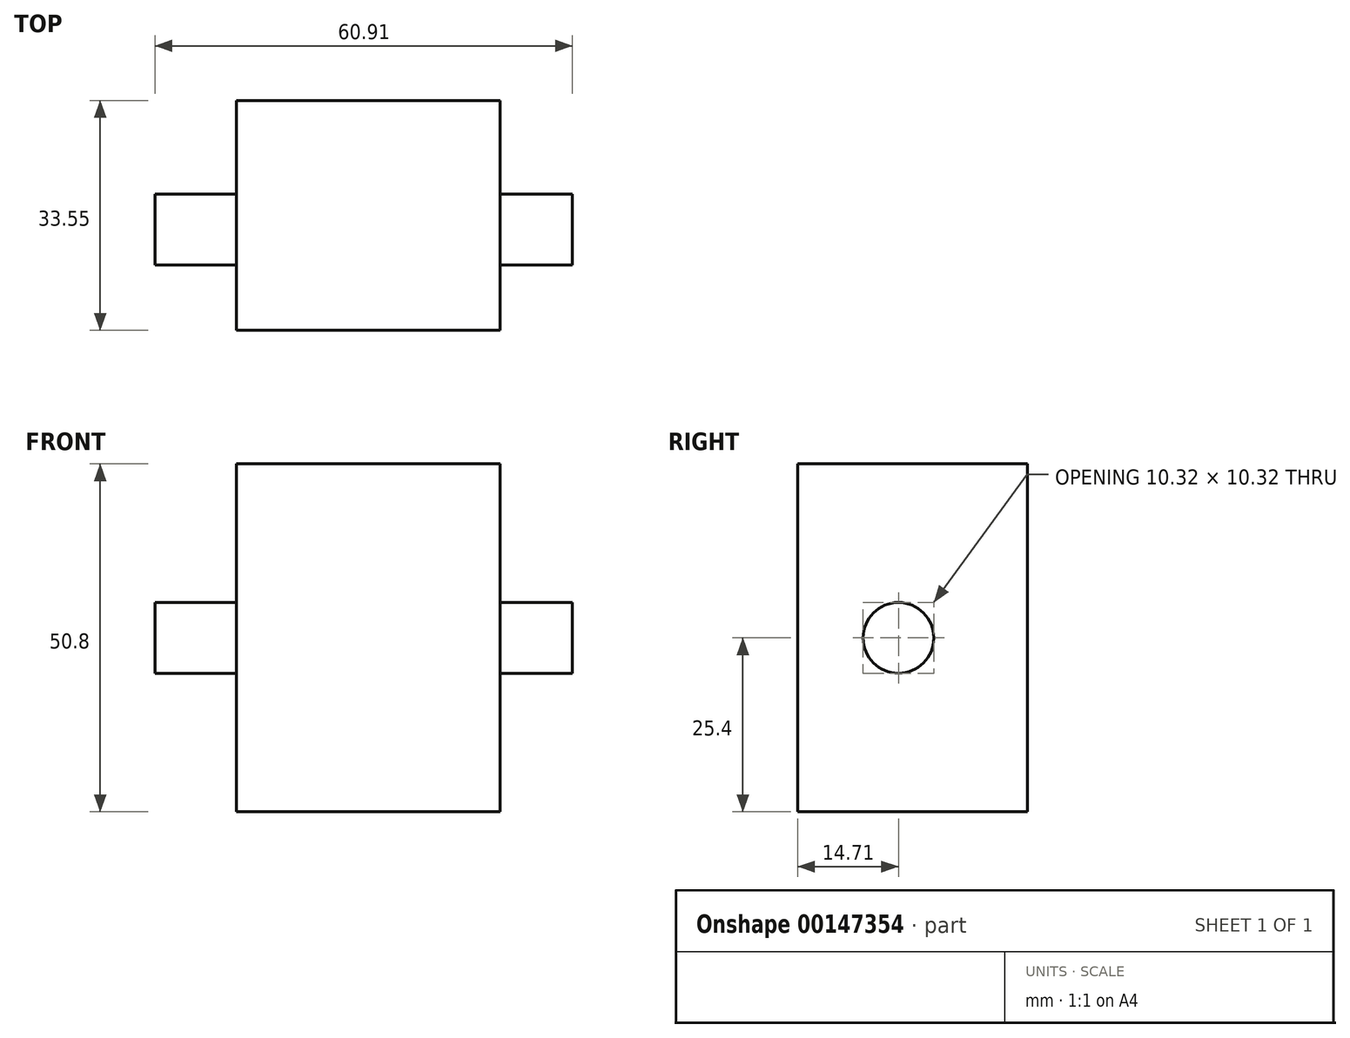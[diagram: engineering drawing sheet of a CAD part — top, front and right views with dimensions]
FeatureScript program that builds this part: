
annotation { "Feature Type Name" : "Feature", "Feature Type Description" : "" }
export const myFeature = defineFeature(function(context is Context, id is Id, definition is map)
    precondition{}
    {
        {
            var Q0;
            Q0=qCreatedBy(makeId("Top.planeOp"),FACE);
            var sketch = newSketch(context, id + "F0", { "sketchPlane" : qUnion([Q0])});
            skLineSegment(sketch, "E0.bottom", {"start": v(-18.84, 18.84) * mm, "end": v(19.62, 18.84) * mm});
            skLineSegment(sketch, "E0.top", {"start": v(-18.84, -14.71) * mm, "end": v(19.62, -14.71) * mm});
            skLineSegment(sketch, "E0.left", {"start": v(-18.84, 18.84) * mm, "end": v(-18.84, -14.71) * mm});
            skLineSegment(sketch, "E0.right", {"start": v(19.62, 18.84) * mm, "end": v(19.62, -14.71) * mm});
            skSolve(sketch);
        }
        {
            var Q0;
            Q0 = qSketchRegion(id + "F0", true);
            extrude(context, id + "F1", {"entities" : qUnion([Q0]), "endBound" : BoundingType.SYMMETRIC, "depth" : 50.8 * mm});
        }
        {
            var Q0;
            Q0=qCreatedBy(makeId("Top.planeOp"),FACE);
            var sketch = newSketch(context, id + "F2", { "sketchPlane" : qUnion([Q0])});
            skLineSegment(sketch, "E1.bottom", {"start": v(-30.71, 0) * mm, "end": v(30.2, 0) * mm});
            skLineSegment(sketch, "E1.top", {"start": v(-30.71, 5.16) * mm, "end": v(30.2, 5.16) * mm});
            skLineSegment(sketch, "E1.left", {"start": v(-30.71, 0) * mm, "end": v(-30.71, 5.16) * mm});
            skLineSegment(sketch, "E1.right", {"start": v(30.2, 0) * mm, "end": v(30.2, 5.16) * mm});
            skSolve(sketch);
        }
        {
            var Q0;
            Q0=makeQuery(id+"F2.imprint","IMPRINT",FACE,{"disambiguationData":[TD([[makeQuery(id+"F2.imprint","IMPRINT",EDGE,{"derivedFrom":sQuery(id+"F2.wireOp",EDGE,"E1.bottom")}),1.0]])]});
            var Q1;
            Q1=sQuery(id+"F2.wireOp",EDGE,"E1.bottom");
            revolve(context, id + "F3", {"operationType" : NewBodyOperationType.ADD, "entities" : qUnion([Q0]), "axis" : qUnion([Q1]), "revolveType" : RevolveType.FULL});
        }
    });
